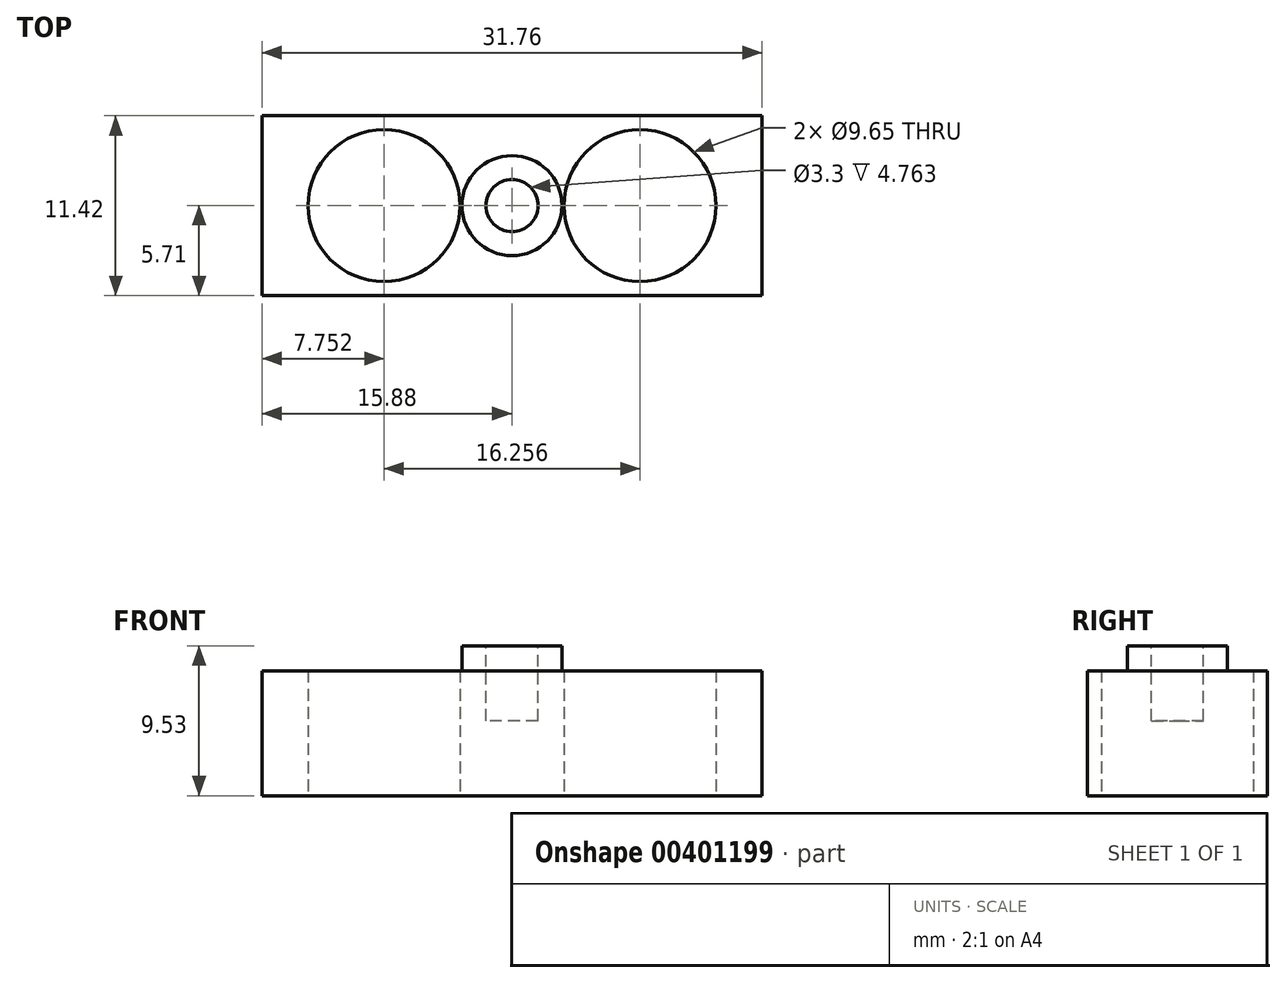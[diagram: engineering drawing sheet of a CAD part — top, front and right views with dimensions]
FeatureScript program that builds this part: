
annotation { "Feature Type Name" : "Feature", "Feature Type Description" : "" }
export const myFeature = defineFeature(function(context is Context, id is Id, definition is map)
    precondition{}
    {
        {
            var Q0;
            Q0=qCreatedBy(makeId("Top.planeOp"),FACE);
            var sketch = newSketch(context, id + "F0", { "sketchPlane" : qUnion([Q0])});
            skLineSegment(sketch, "E0.bottom", {"start": v(-15.88, 5.71) * mm, "end": v(15.88, 5.71) * mm});
            skLineSegment(sketch, "E0.top", {"start": v(-15.88, -5.71) * mm, "end": v(15.88, -5.71) * mm});
            skLineSegment(sketch, "E0.left", {"start": v(-15.88, 5.71) * mm, "end": v(-15.88, -5.72) * mm});
            skLineSegment(sketch, "E0.right", {"start": v(15.88, 5.71) * mm, "end": v(15.88, -5.72) * mm});
            skPoint(sketch, "E0.middle", {"position": v(0, 0) * mm});
            skCircle(sketch, "E1", {"center": v(-8.13, 0) * mm, "radius": 4.83 * mm});
            skCircle(sketch, "E2", {"center": v(8.13, 0) * mm, "radius": 4.83 * mm});
            skSolve(sketch);
        }
        {
            var Q0;
            Q0=makeQuery(id+"F0.imprint","IMPRINT",FACE,{"disambiguationData":[TD([[makeQuery(id+"F0.imprint","IMPRINT",EDGE,{"derivedFrom":sQuery(id+"F0.wireOp",EDGE,"E0.bottom")}),-1.0]])]});
            extrude(context, id + "F1", {"entities" : qUnion([Q0]), "depth" : 7.94 * mm});
        }
        {
            var Q0;
            Q0=makeQuery(id+"F1.opExtrude","CAP_FACE",FACE,{"disambiguationData":[OSD([sQuery(id+"F0.wireOp",EDGE,"E0.bottom"),sQuery(id+"F0.wireOp",EDGE,"E0.top"),sQuery(id+"F0.wireOp",EDGE,"E0.left"),sQuery(id+"F0.wireOp",EDGE,"E0.right"),sQuery(id+"F0.wireOp",EDGE,"E1"),sQuery(id+"F0.wireOp",EDGE,"E2")])],"isStart":false});
            var sketch = newSketch(context, id + "F2", { "sketchPlane" : qUnion([Q0])});
            skCircle(sketch, "E3", {"center": v(0, 0) * mm, "radius": 3.17 * mm});
            skSolve(sketch);
        }
        {
            var Q0;
            Q0 = qSketchRegion(id + "F2", true);
            extrude(context, id + "F3", {"entities" : qUnion([Q0]), "operationType" : NewBodyOperationType.ADD, "depth" : 1.59 * mm});
        }
        {
            var Q0;
            Q0=makeQuery(id+"F3.opExtrude","CAP_FACE",FACE,{"disambiguationData":[OSD([sQuery(id+"F2.wireOp",EDGE,"E3")])],"isStart":false});
            var sketch = newSketch(context, id + "F4", { "sketchPlane" : qUnion([Q0])});
            skCircle(sketch, "E4", {"center": v(0, 0) * mm, "radius": 1.65 * mm});
            skSolve(sketch);
        }
        {
            var Q0;
            Q0 = qSketchRegion(id + "F4", true);
            extrude(context, id + "F5", {"entities" : qUnion([Q0]), "operationType" : NewBodyOperationType.REMOVE, "oppositeDirection" : true, "depth" : 4.76 * mm});
        }
    });
